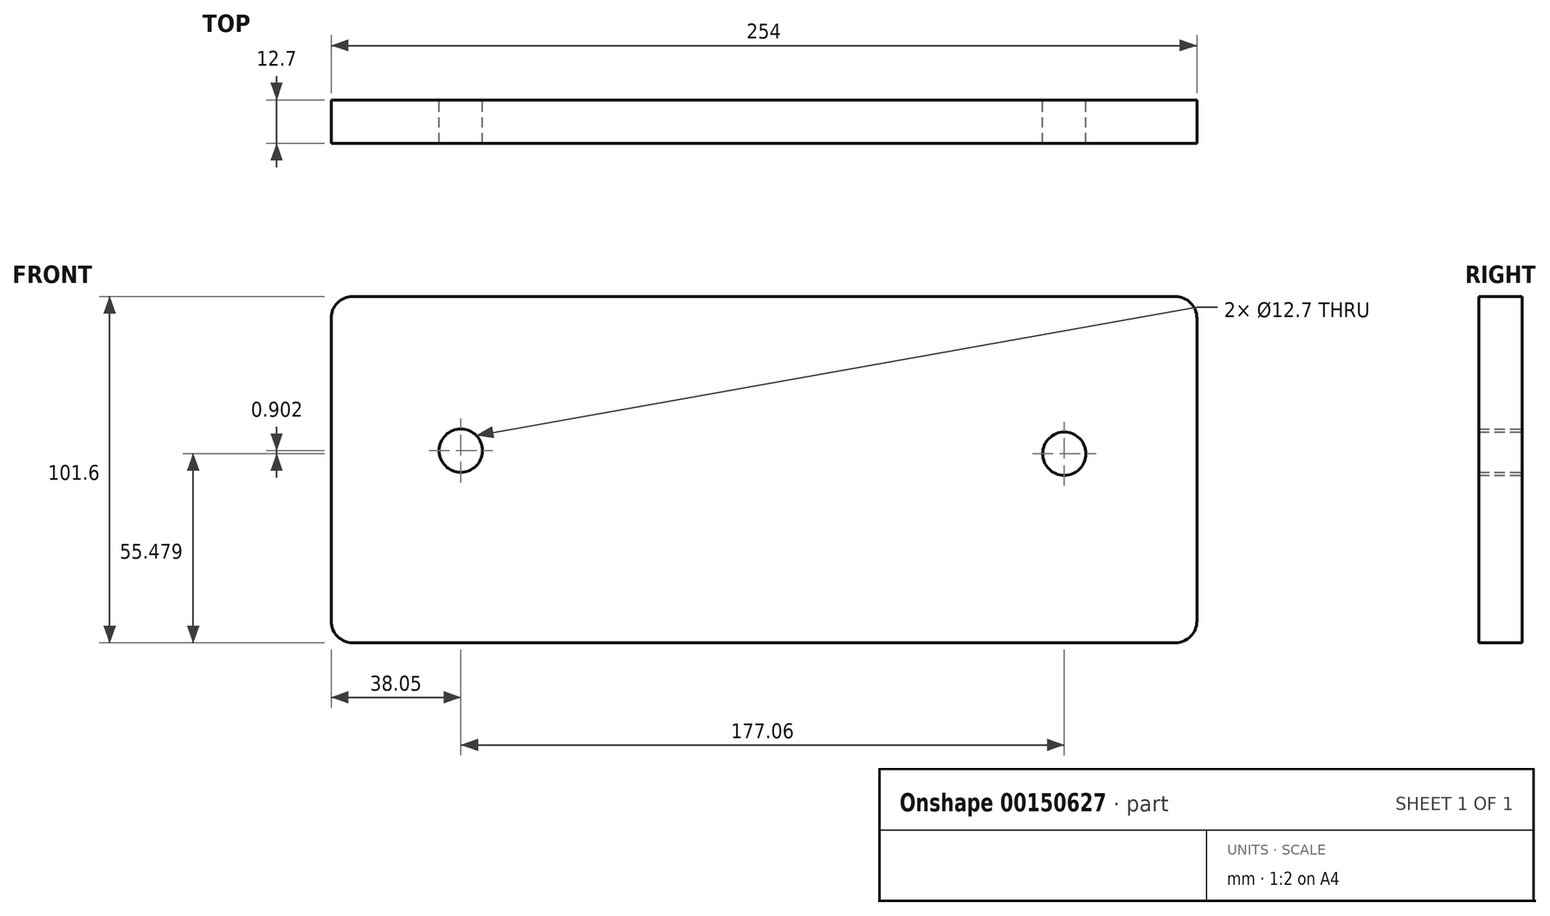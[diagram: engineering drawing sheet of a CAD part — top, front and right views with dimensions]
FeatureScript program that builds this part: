
annotation { "Feature Type Name" : "Feature", "Feature Type Description" : "" }
export const myFeature = defineFeature(function(context is Context, id is Id, definition is map)
    precondition{}
    {
        {
            var Q0;
            Q0=qCreatedBy(makeId("Front.planeOp"),FACE);
            var sketch = newSketch(context, id + "F0", { "sketchPlane" : qUnion([Q0])});
            skLineSegment(sketch, "E0.bottom", {"start": v(6.35, 0) * mm, "end": v(247.65, 0) * mm});
            skLineSegment(sketch, "E0.top", {"start": v(6.35, 101.6) * mm, "end": v(247.65, 101.6) * mm});
            skLineSegment(sketch, "E0.left", {"start": v(0, 6.35) * mm, "end": v(0, 95.25) * mm});
            skLineSegment(sketch, "E0.right", {"start": v(254, 6.35) * mm, "end": v(254, 95.25) * mm});
            skCircle(sketch, "E1", {"center": v(38.05, 56.38) * mm, "radius": 6.35 * mm});
            skCircle(sketch, "E2", {"center": v(215.1, 55.48) * mm, "radius": 6.35 * mm});
            skPoint(sketch, "E3.visualSharp", {"position": v(0, 101.6) * mm});
            skArc(sketch, "E3.filletArc", {"start": v(6.35, 101.6) * mm, "mid": v(1.86, 99.74) * mm, "end": v(0, 95.25) * mm});
            skPoint(sketch, "E4.visualSharp", {"position": v(0, 0) * mm});
            skArc(sketch, "E4.filletArc", {"start": v(0, 6.35) * mm, "mid": v(1.86, 1.86) * mm, "end": v(6.35, 0) * mm});
            skPoint(sketch, "E5.visualSharp", {"position": v(254, 0) * mm});
            skArc(sketch, "E5.filletArc", {"start": v(247.65, 0) * mm, "mid": v(252.14, 1.86) * mm, "end": v(254, 6.35) * mm});
            skPoint(sketch, "E6.visualSharp", {"position": v(254, 101.6) * mm});
            skArc(sketch, "E6.filletArc", {"start": v(254, 95.25) * mm, "mid": v(252.14, 99.74) * mm, "end": v(247.65, 101.6) * mm});
            skSolve(sketch);
        }
        {
            var Q0;
            Q0=makeQuery(id+"F0.imprint","IMPRINT",FACE,{"disambiguationData":[TD([[makeQuery(id+"F0.imprint","IMPRINT",EDGE,{"derivedFrom":sQuery(id+"F0.wireOp",EDGE,"E0.bottom")}),1.0]])]});
            extrude(context, id + "F1", {"entities" : qUnion([Q0]), "depth" : 12.7 * mm});
        }
    });
